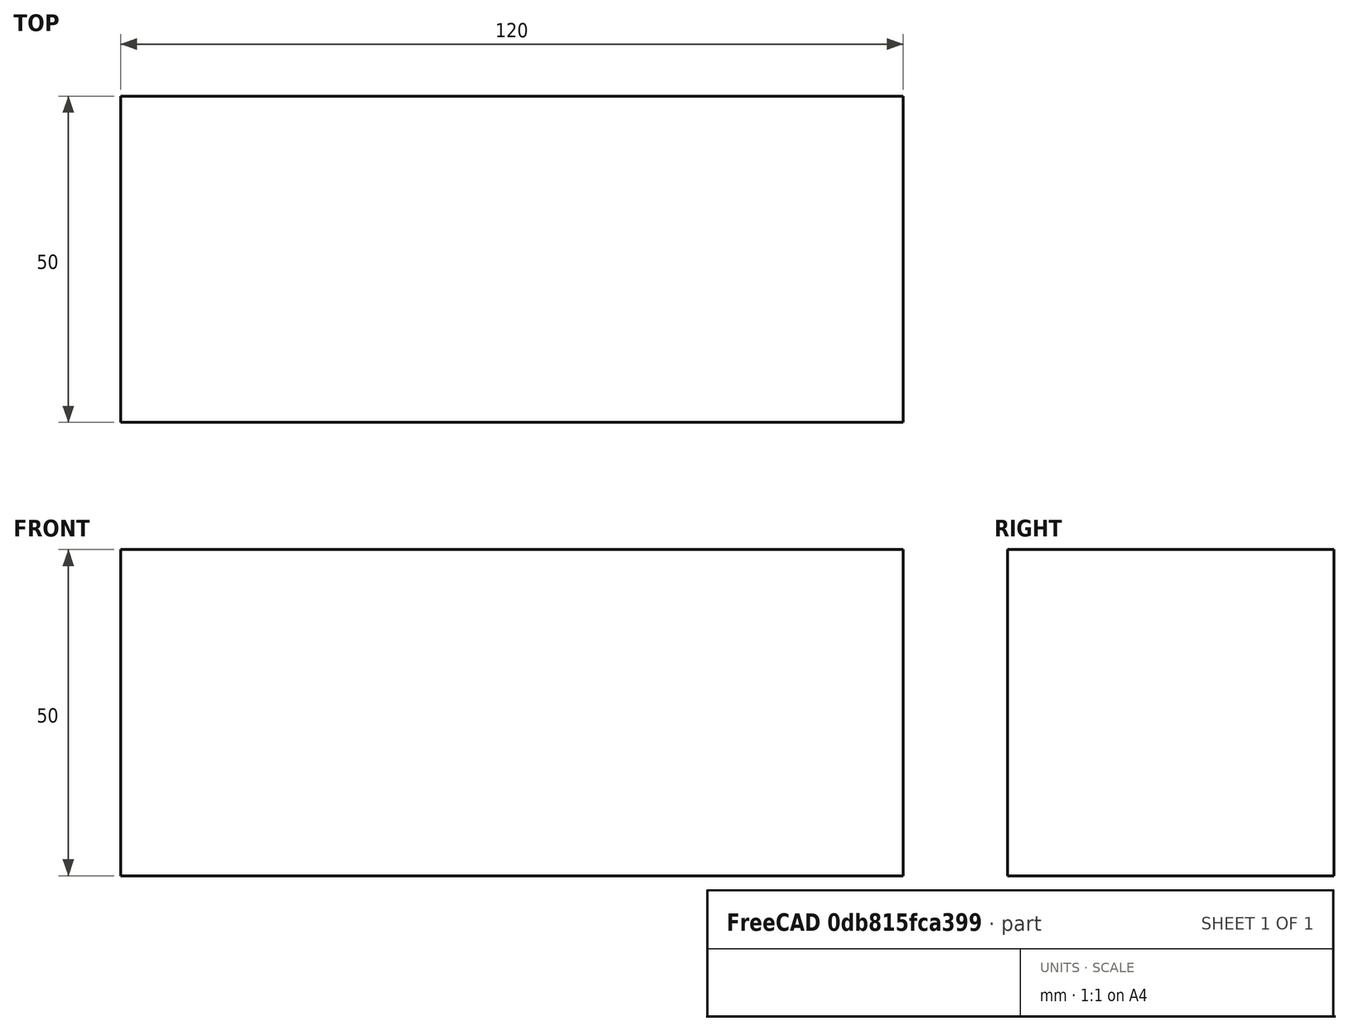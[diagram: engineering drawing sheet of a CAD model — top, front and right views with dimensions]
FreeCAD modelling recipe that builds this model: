
FCSTD DOCUMENT  (FreeCAD 0.15R4671 (Git))
Label: Flat Bar 120x50 EN10058 S235JR
License: All rights reserved
LicenseURL: http://en.wikipedia.org/wiki/All_rights_reserved
objects: Sketcher::SketchObject×1, Part::Extrusion×1
note: 2 computed .brp shape members not serialized (recipe doc carries the construction recipe); baked Part::Feature solids carry a one-line shape summary decoded from their .brp

FEATURE [Sketcher::SketchObject] Sketch
  sketch-geometry (4):
    g0: LineSegment StartX=-60 StartY=-25 StartZ=0 EndX=60 EndY=-25 EndZ=0
    g1: LineSegment StartX=60 StartY=-25 StartZ=0 EndX=60 EndY=25 EndZ=0
    g2: LineSegment StartX=60 StartY=25 StartZ=0 EndX=-60 EndY=25 EndZ=0
    g3: LineSegment StartX=-60 StartY=25 StartZ=0 EndX=-60 EndY=-25 EndZ=0
  constraints (12):
    c: Coincident(g0,g1)
    c: Coincident(g1,g2)
    c: Coincident(g2,g3)
    c: Coincident(g3,g0)
    c: Horizontal(g0)
    c: Horizontal(g2)
    c: Vertical(g1)
    c: Vertical(g3)
    c: Symmetric(g1,g2,g-2)
    c: Symmetric(g0,g1,g-1)
    c: DistanceY(g1) = 50
    c: DistanceX(g0) = 120
FEATURE [Part::Extrusion] Extrude  label="Flat Bar 120x50 EN10058 S235JR"
  Base = -> Sketch
  Dir = (0,0,50)
  Solid = true
